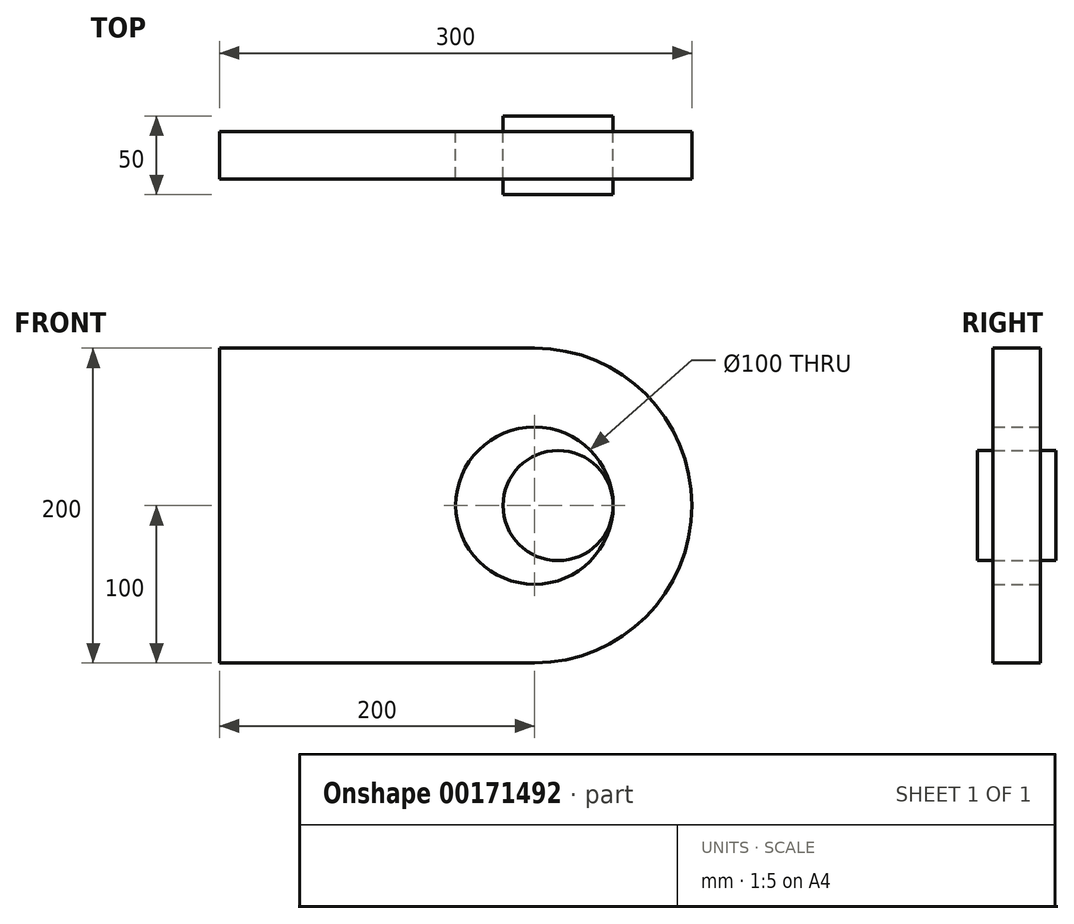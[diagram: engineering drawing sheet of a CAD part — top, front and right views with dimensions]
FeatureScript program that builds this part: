
annotation { "Feature Type Name" : "Feature", "Feature Type Description" : "" }
export const myFeature = defineFeature(function(context is Context, id is Id, definition is map)
    precondition{}
    {
        {
            var Q0;
            Q0=qCreatedBy(makeId("Front.planeOp"),FACE);
            var sketch = newSketch(context, id + "F0", { "sketchPlane" : qUnion([Q0])});
            skLineSegment(sketch, "E0.bottom", {"start": v(0, 0) * mm, "end": v(200, 0) * mm});
            skLineSegment(sketch, "E0.top", {"start": v(0, 200) * mm, "end": v(200, 200) * mm});
            skLineSegment(sketch, "E0.left", {"start": v(0, 0) * mm, "end": v(0, 200) * mm});
            skLineSegment(sketch, "E0.right", {"start": v(200, 0) * mm, "end": v(200, 200) * mm, "construction": true});
            skArc(sketch, "E1", {"start": v(200, 0) * mm, "mid": v(300, 100) * mm, "end": v(200, 200) * mm});
            skCircle(sketch, "E2", {"center": v(200, 100) * mm, "radius": 50 * mm});
            skCircle(sketch, "E3", {"center": v(215, 100) * mm, "radius": 35 * mm});
            skSolve(sketch);
        }
        {
            var Q0;
            Q0=makeQuery(id+"F0.imprint","IMPRINT",FACE,{"disambiguationData":[TD([[makeQuery(id+"F0.imprint","IMPRINT",EDGE,{"derivedFrom":sQuery(id+"F0.wireOp",EDGE,"E0.bottom")}),1.0]])]});
            extrude(context, id + "F1", {"entities" : qUnion([Q0]), "depth" : 30 * mm});
        }
        {
            var Q0;
            Q0=makeQuery(id+"F0.imprint","IMPRINT",FACE,{"disambiguationData":[TD([[makeQuery(id+"F0.imprint","IMPRINT",EDGE,{"derivedFrom":sQuery(id+"F0.wireOp",EDGE,"E3")}),1.0]])]});
            extrude(context, id + "F2", {"entities" : qUnion([Q0]), "depth" : 40 * mm, "hasSecondDirection" : true, "secondDirectionOppositeDirection" : true, "secondDirectionDepth" : 10 * mm});
        }
    });
